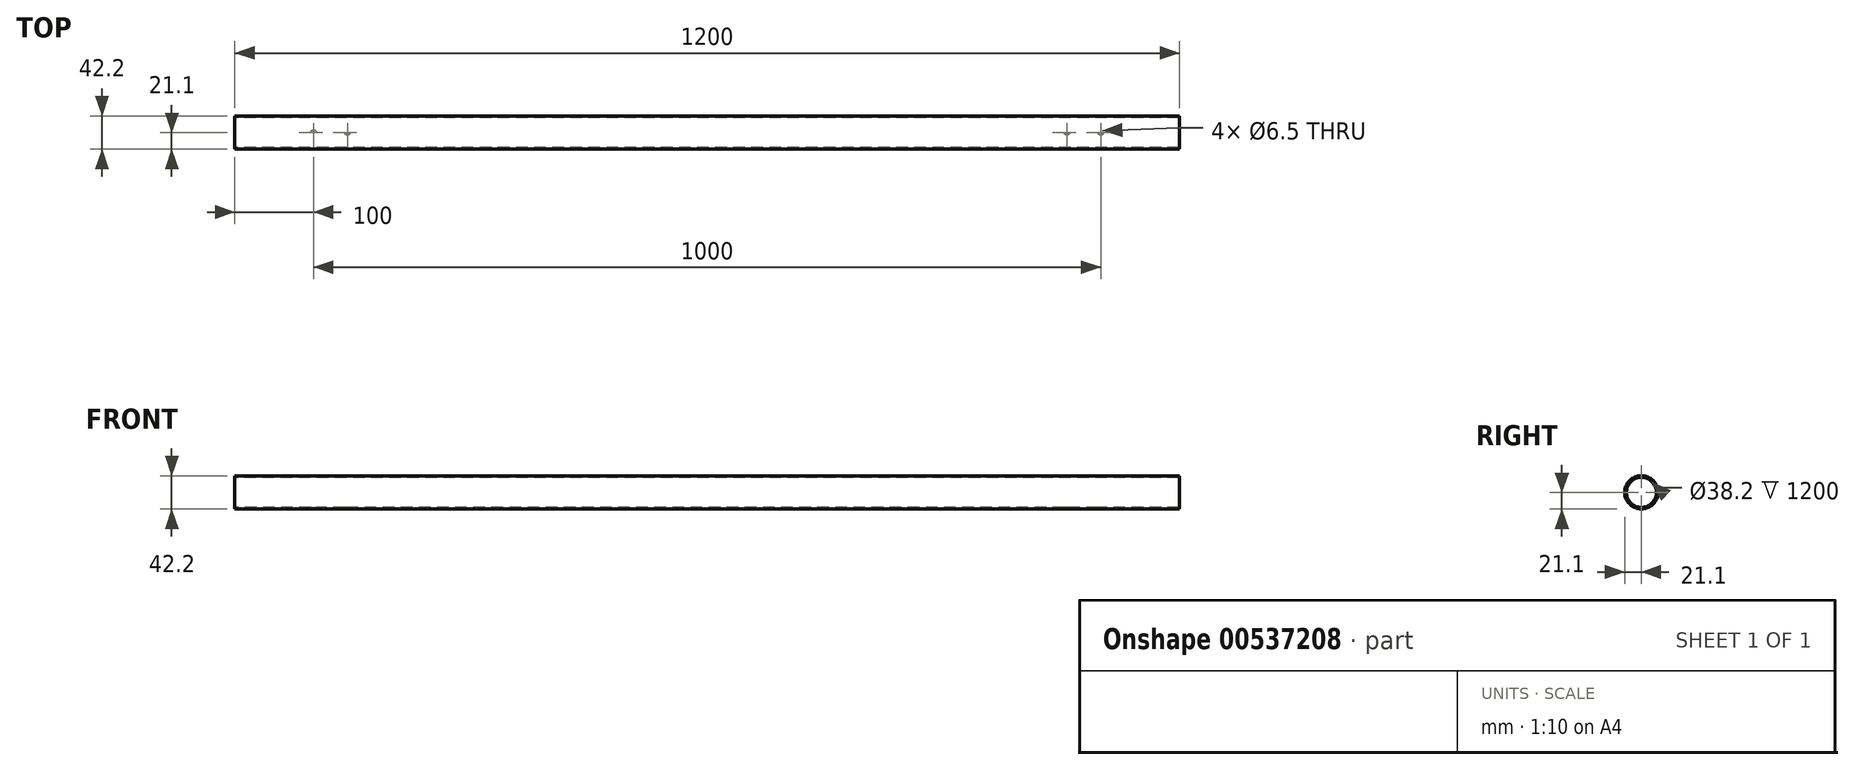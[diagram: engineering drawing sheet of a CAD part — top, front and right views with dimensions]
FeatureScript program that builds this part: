
annotation { "Feature Type Name" : "Feature", "Feature Type Description" : "" }
export const myFeature = defineFeature(function(context is Context, id is Id, definition is map)
    precondition{}
    {
        {
            var Q0;
            Q0=qCreatedBy(makeId("Right.planeOp"),FACE);
            var sketch = newSketch(context, id + "F0", { "sketchPlane" : qUnion([Q0])});
            skCircle(sketch, "E0", {"center": v(0, 0) * mm, "radius": 21.1 * mm});
            skCircle(sketch, "E1", {"center": v(0, 0) * mm, "radius": 19.1 * mm});
            skSolve(sketch);
        }
        {
            var Q0;
            Q0=makeQuery(id+"F0.imprint","IMPRINT",FACE,{"disambiguationData":[TD([[makeQuery(id+"F0.imprint","IMPRINT",EDGE,{"derivedFrom":sQuery(id+"F0.wireOp",EDGE,"E0")}),1.0]])]});
            extrude(context, id + "F1", {"entities" : qUnion([Q0]), "endBound" : BoundingType.SYMMETRIC, "depth" : 1200 * mm, "offsetDistance" : 25 * mm});
        }
        {
            var Q0;
            Q0=qCreatedBy(makeId("Top.planeOp"),FACE);
            cPlane(context, id + "F2", {"entities" : qUnion([Q0]), "cplaneType" : CPlaneType.OFFSET, "offset" : 25 * mm, "oppositeDirection" : true, "width" : 150 * mm, "height" : 150 * mm});
        }
        {
            var Q0;
            Q0=qCreatedBy(id+"F2.planeOp",FACE);
            var sketch = newSketch(context, id + "F3", { "sketchPlane" : qUnion([Q0])});
            skPoint(sketch, "E2", {"position": v(-500, 0) * mm});
            skPoint(sketch, "E3", {"position": v(-457, 0) * mm});
            skPoint(sketch, "E4.MirrorP", {"position": v(500, 0) * mm});
            skPoint(sketch, "E5.MirrorP", {"position": v(457, 0) * mm});
            skSolve(sketch);
        }
        {
            var Q0;
            Q0=sQuery(id+"F3.wireOp",VERTEX,"E2");
            var Q1;
            Q1=sQuery(id+"F3.wireOp",VERTEX,"E3");
            var Q2;
            Q2=sQuery(id+"F3.wireOp",VERTEX,"E5.MirrorP");
            var Q3;
            Q3=sQuery(id+"F3.wireOp",VERTEX,"E4.MirrorP");
            var Q4;
            Q4=makeQuery(id+"F1.opExtrude","SWEPT_BODY",BODY,{"disambiguationData":[OSD([sQuery(id+"F0.wireOp",EDGE,"E0"),sQuery(id+"F0.wireOp",EDGE,"E1")])]});
            hole(context, id + "F4", {"style" : HoleStyle.SIMPLE, "endStyle" : HoleEndStyle.BLIND, "oppositeDirection" : true, "holeDiameter" : 6.5 * mm, "holeDepth" : 10 * mm, "isTappedThrough" : true, "tappedDepth" : 12 * mm, "tapClearance" : 3, "locations" : qUnion([Q0, Q1, Q2, Q3]), "scope" : qUnion([Q4])});
        }
    });
